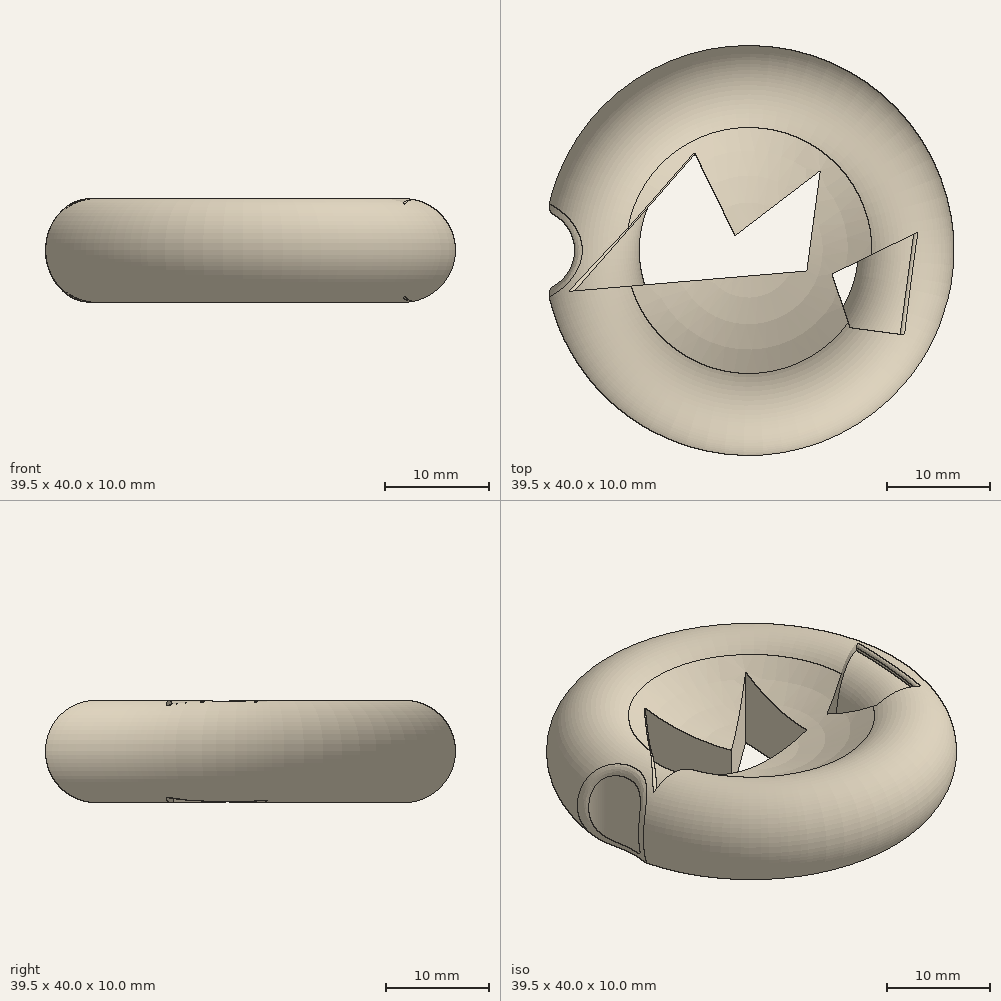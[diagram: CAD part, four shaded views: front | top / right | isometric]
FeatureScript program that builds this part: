
annotation { "Feature Type Name" : "Feature", "Feature Type Description" : "" }
export const myFeature = defineFeature(function(context is Context, id is Id, definition is map)
    precondition{}
    {
        {
            var Q0;
            Q0=qCreatedBy(makeId("Front.planeOp"),FACE);
            var sketch = newSketch(context, id + "F0", { "sketchPlane" : qUnion([Q0])});
            skArc(sketch, "E0", {"start": v(-12, 9) * mm, "mid": v(-19.74, 6.58) * mm, "end": v(-15, 0) * mm});
            skArc(sketch, "E1", {"start": v(-12, 9) * mm, "mid": v(-6.32, 6.03) * mm, "end": v(0, 5) * mm});
            skLineSegment(sketch, "E2", {"start": v(0, 0) * mm, "end": v(-15, 0) * mm});
            skLineSegment(sketch, "E3", {"start": v(0, 0) * mm, "end": v(0, 5) * mm});
            skSolve(sketch);
        }
        {
            var Q0;
            Q0 = qSketchRegion(id + "F0", true);
            var Q1;
            Q1=sQuery(id+"F0.wireOp",EDGE,"E3");
            revolve(context, id + "F1", {"entities" : qUnion([Q0]), "axis" : qUnion([Q1]), "revolveType" : RevolveType.FULL});
        }
        {
            var Q0;
            Q0=qCreatedBy(makeId("Top.planeOp"),FACE);
            cPlane(context, id + "F2", {"entities" : qUnion([Q0]), "cplaneType" : CPlaneType.OFFSET, "offset" : 10 * mm, "width" : 150 * mm, "height" : 150 * mm});
        }
        {
            var Q0;
            Q0=qCreatedBy(id+"F2.planeOp",FACE);
            var sketch = newSketch(context, id + "F3", { "sketchPlane" : qUnion([Q0])});
            skLineSegment(sketch, "E4", {"start": v(-16.96, -3.94) * mm, "end": v(-5.24, 9.4) * mm});
            skLineSegment(sketch, "E5", {"start": v(-5.24, 9.4) * mm, "end": v(-1.34, 1.42) * mm});
            skLineSegment(sketch, "E6", {"start": v(-1.34, 1.42) * mm, "end": v(6.96, 7.76) * mm});
            skLineSegment(sketch, "E7", {"start": v(6.96, 7.76) * mm, "end": v(5.65, -2) * mm});
            skLineSegment(sketch, "E8", {"start": v(5.65, -2) * mm, "end": v(-16.96, -3.94) * mm});
            skLineSegment(sketch, "E9", {"start": v(8.1, -2.33) * mm, "end": v(16.07, 1.57) * mm});
            skLineSegment(sketch, "E10", {"start": v(16.07, 1.57) * mm, "end": v(14.76, -8.18) * mm});
            skLineSegment(sketch, "E11", {"start": v(14.76, -8.18) * mm, "end": v(9.88, -7.53) * mm});
            skLineSegment(sketch, "E12", {"start": v(9.88, -7.53) * mm, "end": v(8.1, -2.33) * mm});
            skLineSegment(sketch, "E13.0", {"start": v(-16.96, -3.94) * mm, "end": v(-16.96, -3.94) * mm});
            skLineSegment(sketch, "E13.1", {"start": v(-16.96, -3.94) * mm, "end": v(14.76, -8.18) * mm, "construction": true});
            skSolve(sketch);
        }
        {
            var Q0;
            Q0 = qSketchRegion(id + "F3", true);
            extrude(context, id + "F4", {"entities" : qUnion([Q0]), "operationType" : NewBodyOperationType.REMOVE, "endBound" : BoundingType.THROUGH_ALL, "oppositeDirection" : true, "depth" : 25 * mm, "offsetDistance" : 25 * mm});
        }
        {
            var Q0;
            Q0=qCreatedBy(makeId("Front.planeOp"),FACE);
            var sketch = newSketch(context, id + "F5", { "sketchPlane" : qUnion([Q0])});
            skCircle(sketch, "E14", {"center": v(-15, 5) * mm, "radius": 4.3 * mm});
            skCircle(sketch, "E15.0", {"center": v(-15, 5) * mm, "radius": 3.9 * mm});
            skSolve(sketch);
        }
        {
            var Q0;
            Q0 = qSketchRegion(id + "F5", true);
            var Q1;
            Q1=sQuery(id+"F0.wireOp",EDGE,"E3");
            revolve(context, id + "F6", {"operationType" : NewBodyOperationType.ADD, "entities" : qUnion([Q0]), "axis" : qUnion([Q1]), "revolveType" : RevolveType.FULL});
        }
        {
            var Q0;
            Q0=qCreatedBy(makeId("Top.planeOp"),FACE);
            var sketch = newSketch(context, id + "F7", { "sketchPlane" : qUnion([Q0])});
            skCircle(sketch, "E16", {"center": v(-21, 0) * mm, "radius": 4 * mm});
            skSolve(sketch);
        }
        {
            var Q0;
            Q0 = qSketchRegion(id + "F7", true);
            extrude(context, id + "F8", {"entities" : qUnion([Q0]), "operationType" : NewBodyOperationType.REMOVE, "depth" : 25 * mm, "offsetDistance" : 25 * mm});
        }
        {
            var Q0;
            Q0=makeQuery(id+"F8.boolean.opBoolean","INTERSECT",EDGE,{"derivedFrom":[makeQuery(id+"F1.opRevolve","SWEPT_FACE",FACE,{"disambiguationData":[OSD([sQuery(id+"F0.wireOp",EDGE,"E0")])]}),makeQuery(id+"F8.opExtrude","SWEPT_FACE",FACE,{"disambiguationData":[OSD([sQuery(id+"F7.wireOp",EDGE,"E16")])]})]});
            fillet(context, id + "F9", {"entities" : qUnion([Q0]), "radius" : 1 * mm, "tangentPropagation" : true, "allowEdgeOverflow" : false});
        }
        {
            var Q0;
            Q0=makeQuery(id+"F4.boolean.opBoolean","INTERSECT",EDGE,{"disambiguationData":[OD(1.0)],"derivedFrom":[makeQuery(id+"F1.opRevolve","SWEPT_FACE",FACE,{"disambiguationData":[OSD([sQuery(id+"F0.wireOp",EDGE,"E0")])]}),makeQuery(id+"F4.opExtrude","SWEPT_FACE",FACE,{"disambiguationData":[OSD([sQuery(id+"F3.wireOp",EDGE,"E10")])]})]});
            var Q1;
            Q1=makeQuery(id+"F4.boolean.opBoolean","INTERSECT",EDGE,{"derivedFrom":[makeQuery(id+"F1.opRevolve","SWEPT_FACE",FACE,{"disambiguationData":[OSD([sQuery(id+"F0.wireOp",EDGE,"E2")])]}),makeQuery(id+"F4.opExtrude","SWEPT_FACE",FACE,{"disambiguationData":[OSD([sQuery(id+"F3.wireOp",EDGE,"E4")])]})]});
            fillet(context, id + "F10", {"entities" : qUnion([Q0, Q1]), "radius" : .3 * mm, "tangentPropagation" : true, "allowEdgeOverflow" : false});
        }
        {
            var Q0;
            Q0=makeQuery(id+"F4.boolean.opBoolean","INTERSECT",EDGE,{"disambiguationData":[OD(0.0)],"derivedFrom":[makeQuery(id+"F1.opRevolve","SWEPT_FACE",FACE,{"disambiguationData":[OSD([sQuery(id+"F0.wireOp",EDGE,"E0")])]}),makeQuery(id+"F4.opExtrude","SWEPT_FACE",FACE,{"disambiguationData":[OSD([sQuery(id+"F3.wireOp",EDGE,"E10")])]})]});
            var Q1;
            Q1=makeQuery(id+"F4.boolean.opBoolean","INTERSECT",EDGE,{"derivedFrom":[makeQuery(id+"F1.opRevolve","SWEPT_FACE",FACE,{"disambiguationData":[OSD([sQuery(id+"F0.wireOp",EDGE,"E1")])]}),makeQuery(id+"F4.opExtrude","SWEPT_FACE",FACE,{"disambiguationData":[OSD([sQuery(id+"F3.wireOp",EDGE,"E4")])]})]});
            fillet(context, id + "F11", {"entities" : qUnion([Q0, Q1]), "radius" : .3 * mm, "tangentPropagation" : true, "allowEdgeOverflow" : false});
        }
    });
